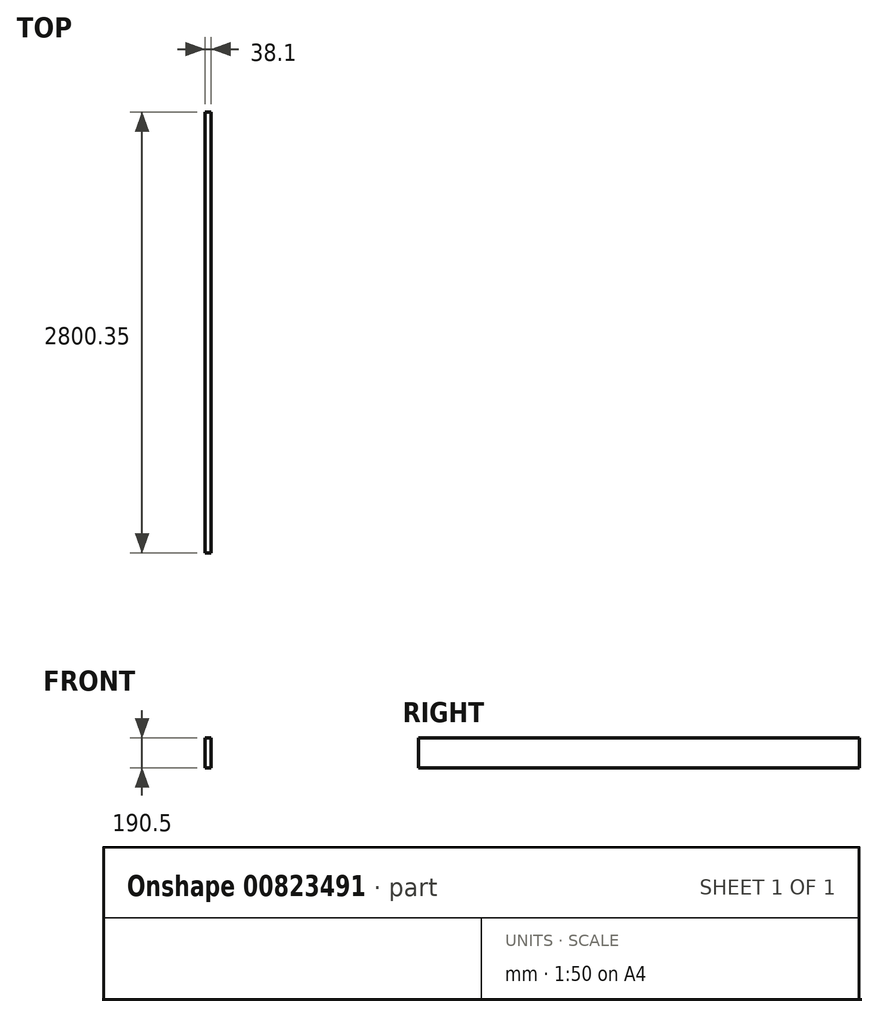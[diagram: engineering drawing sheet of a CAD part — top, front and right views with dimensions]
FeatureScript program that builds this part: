
annotation { "Feature Type Name" : "Feature", "Feature Type Description" : "" }
export const myFeature = defineFeature(function(context is Context, id is Id, definition is map)
    precondition{}
    {
        {
            var Q0;
            Q0=qCreatedBy(makeId("Front.planeOp"),FACE);
            var sketch = newSketch(context, id + "F0", { "sketchPlane" : qUnion([Q0])});
            skLineSegment(sketch, "E0.bottom", {"start": v(0, 0) * mm, "end": v(38.1, 0) * mm});
            skLineSegment(sketch, "E0.top", {"start": v(0, 190.5) * mm, "end": v(38.1, 190.5) * mm});
            skLineSegment(sketch, "E0.left", {"start": v(0, 0) * mm, "end": v(0, 190.5) * mm});
            skLineSegment(sketch, "E0.right", {"start": v(38.1, 0) * mm, "end": v(38.1, 190.5) * mm});
            skSolve(sketch);
        }
        {
            var Q0;
            Q0=qSketchRegion(id+"F0",true);
            extrude(context, id + "F1", {"entities" : qUnion([Q0]), "depth" : 2800.35 * mm, "offsetDistance" : 25.4 * mm});
        }
    });
